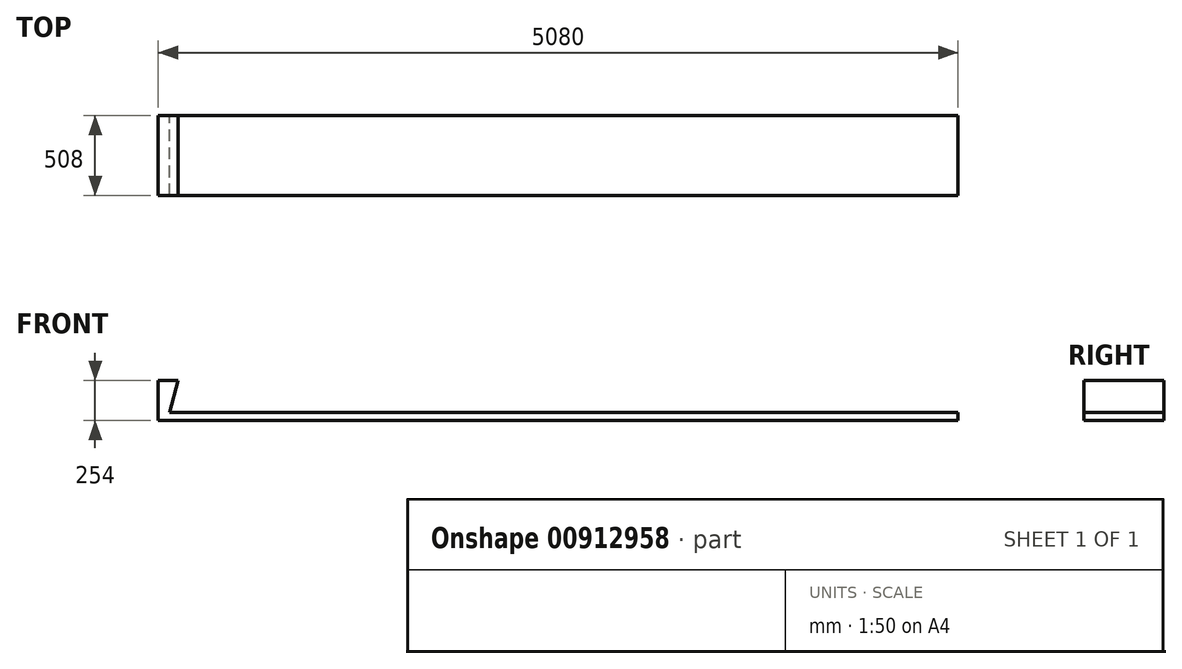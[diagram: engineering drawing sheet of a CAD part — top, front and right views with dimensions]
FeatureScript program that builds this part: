
annotation { "Feature Type Name" : "Feature", "Feature Type Description" : "" }
export const myFeature = defineFeature(function(context is Context, id is Id, definition is map)
    precondition{}
    {
        {
            var Q0;
            Q0=qCreatedBy(makeId("Front.planeOp"),FACE);
            var sketch = newSketch(context, id + "F0", { "sketchPlane" : qUnion([Q0])});
            skLineSegment(sketch, "E0", {"start": v(0, 0) * mm, "end": v(54.45, 203.2) * mm});
            skLineSegment(sketch, "E1", {"start": v(54.45, 203.2) * mm, "end": v(-72.55, 203.2) * mm});
            skLineSegment(sketch, "E2", {"start": v(-72.55, 203.2) * mm, "end": v(-72.55, -50.8) * mm});
            skLineSegment(sketch, "E3", {"start": v(-72.55, -50.8) * mm, "end": v(5007.45, -50.8) * mm});
            skLineSegment(sketch, "E4", {"start": v(5007.45, -50.8) * mm, "end": v(5007.45, 0) * mm});
            skLineSegment(sketch, "E5", {"start": v(5007.45, 0) * mm, "end": v(0, 0) * mm});
            skLineSegment(sketch, "E6", {"start": v(0, 0) * mm, "end": v(0, 203.2) * mm, "construction": true});
            skSolve(sketch);
        }
        {
            var Q0;
            Q0 = qSketchRegion(id + "F0", true);
            extrude(context, id + "F1", {"entities" : qUnion([Q0]), "depth" : 508 * mm, "offsetDistance" : 25.4 * mm});
        }
    });
